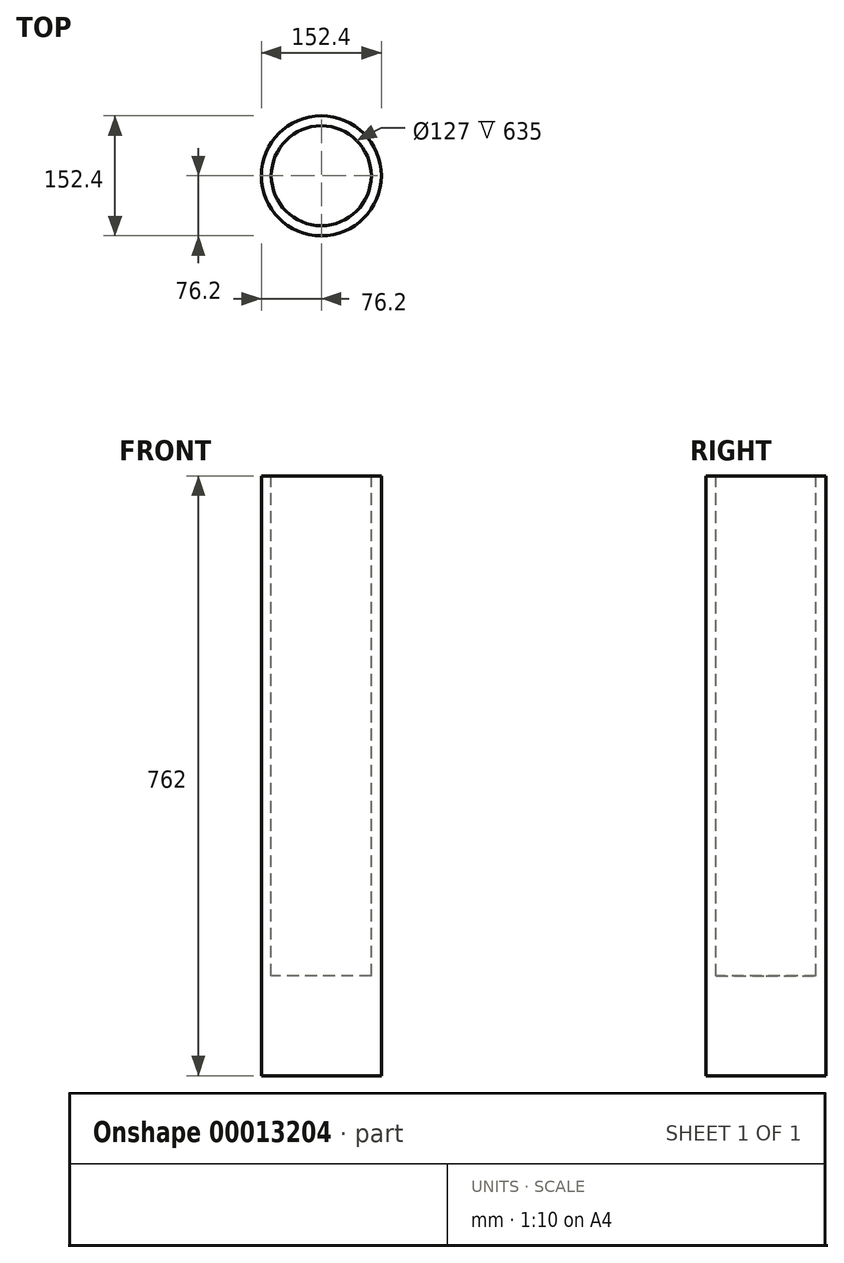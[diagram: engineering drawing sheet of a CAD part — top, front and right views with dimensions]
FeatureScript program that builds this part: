
annotation { "Feature Type Name" : "Feature", "Feature Type Description" : "" }
export const myFeature = defineFeature(function(context is Context, id is Id, definition is map)
    precondition{}
    {
        {
            var Q0;
            Q0=qCreatedBy(makeId("Top.planeOp"),FACE);
            var sketch = newSketch(context, id + "F0", { "sketchPlane" : qUnion([Q0])});
            skCircle(sketch, "E0", {"center": v(0, 0) * mm, "radius": 76.2 * mm});
            skSolve(sketch);
        }
        {
            var Q0;
            Q0 = qSketchRegion(id + "F0", true);
            extrude(context, id + "F1", {"entities" : qUnion([Q0]), "depth" : 762 * mm});
        }
        {
            var Q0;
            Q0=makeQuery(id+"F1.opExtrude","CAP_FACE",FACE,{"disambiguationData":[OSD([sQuery(id+"F0.wireOp",EDGE,"E0")])],"isStart":false});
            var sketch = newSketch(context, id + "F2", { "sketchPlane" : qUnion([Q0])});
            skCircle(sketch, "E1", {"center": v(0, 0) * mm, "radius": 63.5 * mm});
            skSolve(sketch);
        }
        {
            var Q0;
            Q0 = qSketchRegion(id + "F2", true);
            extrude(context, id + "F3", {"entities" : qUnion([Q0]), "operationType" : NewBodyOperationType.REMOVE, "oppositeDirection" : true, "depth" : 635 * mm});
        }
    });
